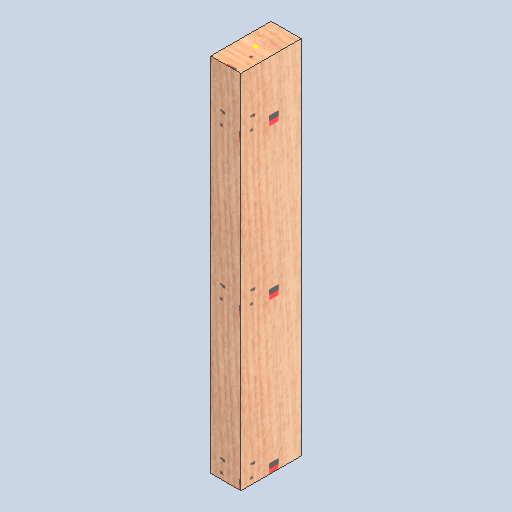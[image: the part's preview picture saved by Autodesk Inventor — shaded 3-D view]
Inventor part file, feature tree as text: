
AUTODESK INVENTOR PART (.ipt)
format: ipt  version: 2025 (Build 290162000, 162)  size: 361,472 bytes
history: native  units: in
note: dims shown in document units (in); Inventor stores cm internally (conversion verified against a paired STEP export)
features: sketch x2, extrude x1
ambient origin geometry x8: Origin, YZ Plane, XZ Plane, XY Plane, X Axis, Y Axis, Z Axis, Center Point
bodies: Solid1 (feature_tree)
feature tree (3):
  extrude  "Extrusion1"  Depth=4.0in
  sketch  "Sketch2"  dims[d2=24.0in d3=0.0in]
  sketch  "Sketch1"  dims[d0=2.0in d1=4.0in]
